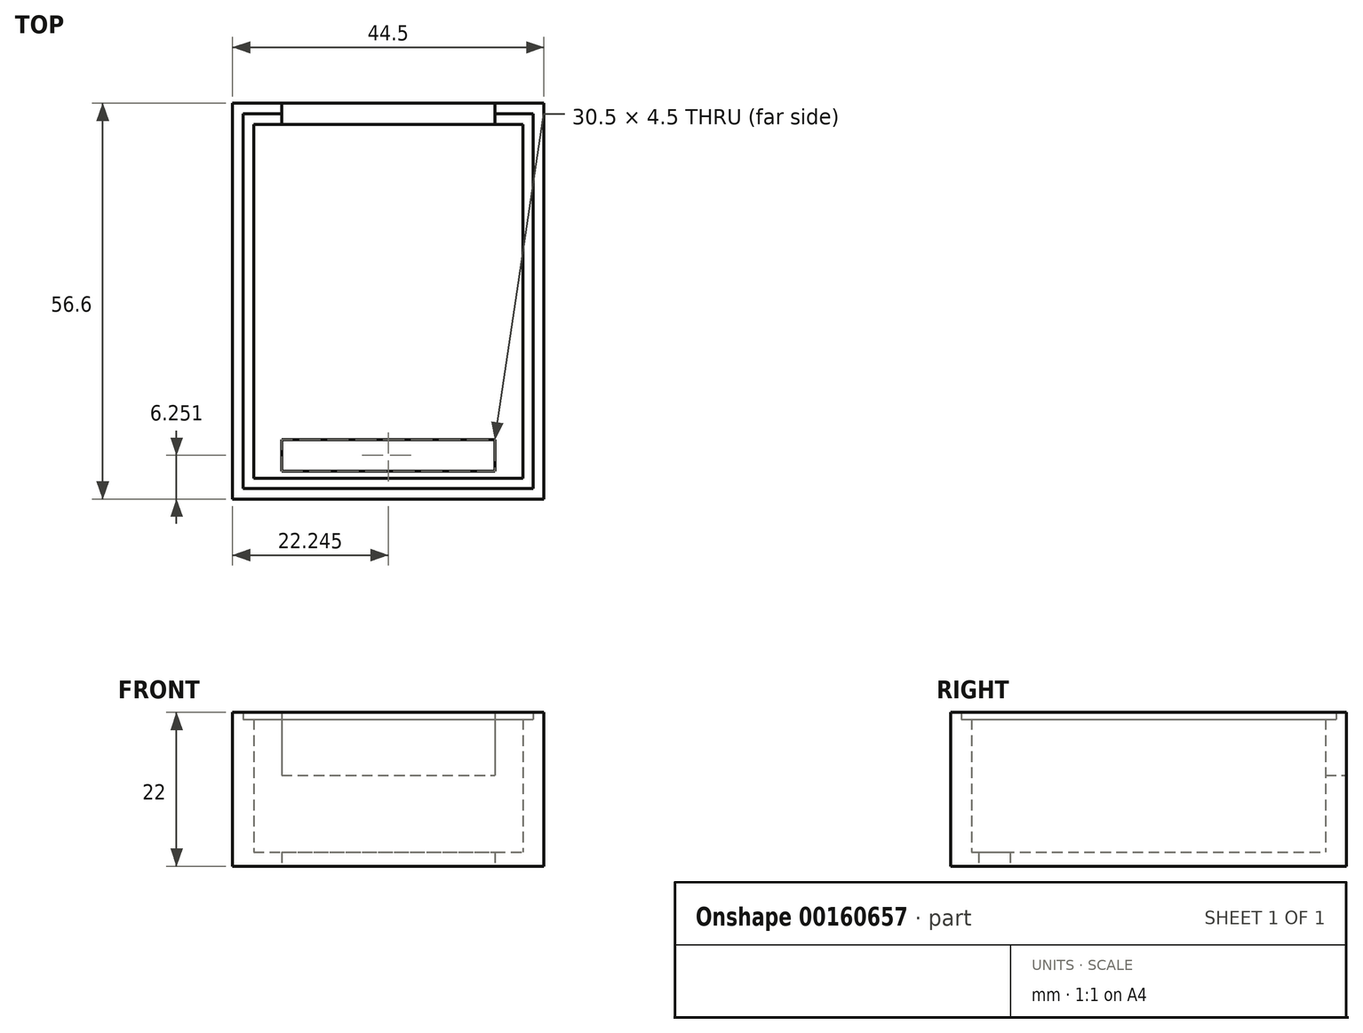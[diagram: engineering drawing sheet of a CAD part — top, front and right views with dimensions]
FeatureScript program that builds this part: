
annotation { "Feature Type Name" : "Feature", "Feature Type Description" : "" }
export const myFeature = defineFeature(function(context is Context, id is Id, definition is map)
    precondition{}
    {
        {
            var Q0;
            Q0=qCreatedBy(makeId("Top.planeOp"),FACE);
            var sketch = newSketch(context, id + "F0", { "sketchPlane" : qUnion([Q0])});
            skLineSegment(sketch, "E0.bottom", {"start": v(-19.27, -25.27) * mm, "end": v(19.23, -25.27) * mm});
            skLineSegment(sketch, "E0.top", {"start": v(-19.27, 25.33) * mm, "end": v(19.23, 25.33) * mm});
            skLineSegment(sketch, "E0.left", {"start": v(-19.27, -25.27) * mm, "end": v(-19.27, 25.33) * mm});
            skLineSegment(sketch, "E0.right", {"start": v(19.23, -25.27) * mm, "end": v(19.23, 25.33) * mm});
            skLineSegment(sketch, "E1.0", {"start": v(-22.27, -28.27) * mm, "end": v(-22.27, 28.33) * mm});
            skLineSegment(sketch, "E1.1", {"start": v(-22.27, -28.27) * mm, "end": v(22.23, -28.27) * mm});
            skLineSegment(sketch, "E1.2", {"start": v(22.23, -28.27) * mm, "end": v(22.23, 28.33) * mm});
            skLineSegment(sketch, "E1.3", {"start": v(-22.27, 28.33) * mm, "end": v(22.23, 28.33) * mm});
            skLineSegment(sketch, "E2.0", {"start": v(20.73, -26.77) * mm, "end": v(20.73, 26.83) * mm});
            skLineSegment(sketch, "E2.1", {"start": v(-20.77, -26.77) * mm, "end": v(20.73, -26.77) * mm});
            skLineSegment(sketch, "E2.2", {"start": v(-20.77, -26.77) * mm, "end": v(-20.77, 26.83) * mm});
            skLineSegment(sketch, "E2.3", {"start": v(-20.77, 26.83) * mm, "end": v(20.73, 26.83) * mm});
            skSolve(sketch);
        }
        {
            var Q0;
            Q0=makeQuery(id+"F0.imprint","IMPRINT",FACE,{"disambiguationData":[TD([[makeQuery(id+"F0.imprint","IMPRINT",EDGE,{"derivedFrom":sQuery(id+"F0.wireOp",EDGE,"E0.bottom")}),1.0]])]});
            extrude(context, id + "F1", {"entities" : qUnion([Q0]), "depth" : 2 * mm});
        }
        {
            var Q0;
            Q0=makeQuery(id+"F0.imprint","IMPRINT",FACE,{"disambiguationData":[TD([[makeQuery(id+"F0.imprint","IMPRINT",EDGE,{"derivedFrom":sQuery(id+"F0.wireOp",EDGE,"E0.bottom")}),-1.0]])]});
            extrude(context, id + "F2", {"entities" : qUnion([Q0]), "operationType" : NewBodyOperationType.ADD, "depth" : 21 * mm});
        }
        {
            var Q0;
            Q0=makeQuery(id+"F0.imprint","IMPRINT",FACE,{"disambiguationData":[TD([[makeQuery(id+"F0.imprint","IMPRINT",EDGE,{"derivedFrom":sQuery(id+"F0.wireOp",EDGE,"E1.0")}),-1.0]])]});
            extrude(context, id + "F3", {"entities" : qUnion([Q0]), "operationType" : NewBodyOperationType.ADD, "depth" : 22 * mm});
        }
        {
            var Q0;
            Q0=makeQuery(id+"F3.opExtrude","SWEPT_FACE",FACE,{"disambiguationData":[OSD([sQuery(id+"F0.wireOp",EDGE,"E1.3")])]});
            var sketch = newSketch(context, id + "F4", { "sketchPlane" : qUnion([Q0])});
            skLineSegment(sketch, "E3.bottom", {"start": v(15.27, 22) * mm, "end": v(-15.23, 22) * mm});
            skLineSegment(sketch, "E3.top", {"start": v(15.27, 13) * mm, "end": v(-15.23, 13) * mm});
            skLineSegment(sketch, "E3.left", {"start": v(15.27, 22) * mm, "end": v(15.27, 13) * mm});
            skLineSegment(sketch, "E3.right", {"start": v(-15.23, 22) * mm, "end": v(-15.23, 13) * mm});
            skSolve(sketch);
        }
        {
            var Q0;
            Q0=makeQuery(id+"F4.imprint","IMPRINT",FACE,{"disambiguationData":[TD([[makeQuery(id+"F4.imprint","IMPRINT",EDGE,{"derivedFrom":sQuery(id+"F4.wireOp",EDGE,"E3.bottom")}),1.0]])]});
            extrude(context, id + "F5", {"entities" : qUnion([Q0]), "operationType" : NewBodyOperationType.REMOVE, "oppositeDirection" : true, "depth" : 4 * mm});
        }
        {
            var Q0;
            Q0=makeQuery(id+"F0.imprint","IMPRINT",FACE,{"disambiguationData":[TD([[makeQuery(id+"F0.imprint","IMPRINT",EDGE,{"derivedFrom":sQuery(id+"F0.wireOp",EDGE,"E0.bottom")}),1.0]])]});
            var sketch = newSketch(context, id + "F6", { "sketchPlane" : qUnion([Q0])});
            skLineSegment(sketch, "E4.bottom", {"start": v(15.23, -19.77) * mm, "end": v(-15.27, -19.77) * mm});
            skLineSegment(sketch, "E4.top", {"start": v(15.23, -24.27) * mm, "end": v(-15.27, -24.27) * mm});
            skLineSegment(sketch, "E4.left", {"start": v(15.23, -19.77) * mm, "end": v(15.23, -24.27) * mm});
            skLineSegment(sketch, "E4.right", {"start": v(-15.27, -19.77) * mm, "end": v(-15.27, -24.27) * mm});
            skSolve(sketch);
        }
        {
            var Q0;
            Q0 = qSketchRegion(id + "F6", true);
            extrude(context, id + "F7", {"entities" : qUnion([Q0]), "operationType" : NewBodyOperationType.REMOVE, "depth" : 4 * mm});
        }
    });
